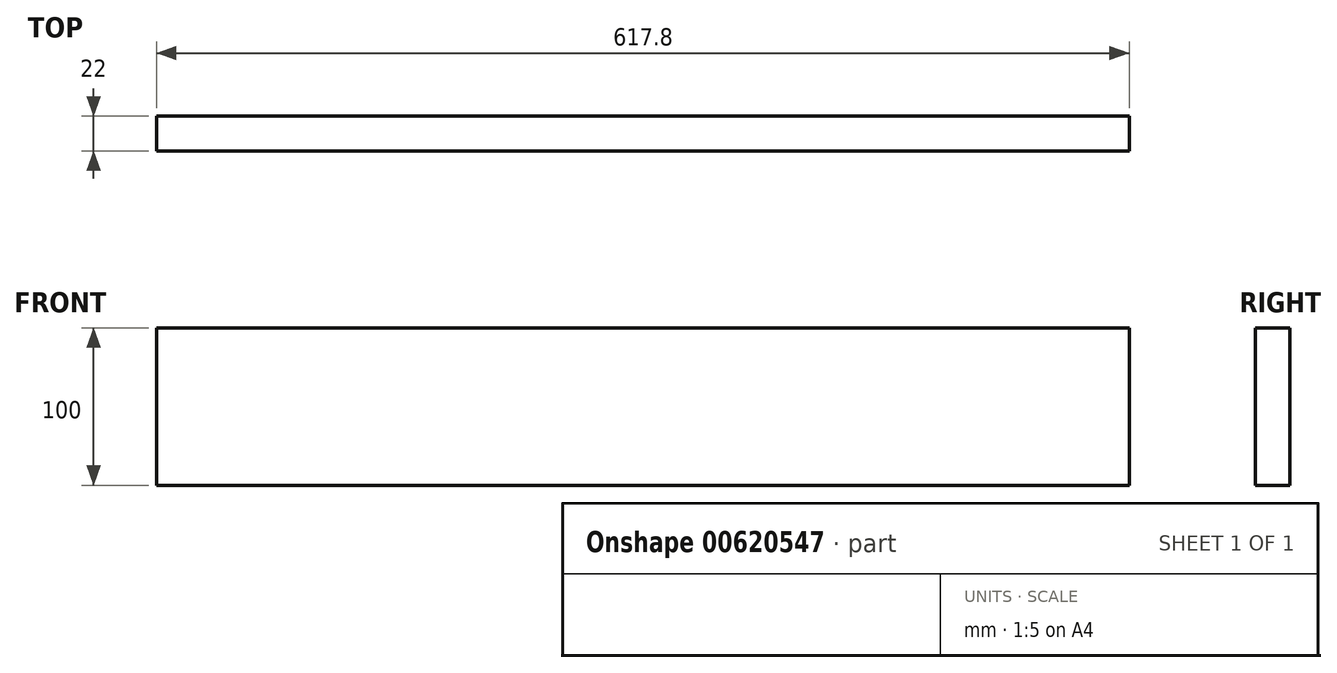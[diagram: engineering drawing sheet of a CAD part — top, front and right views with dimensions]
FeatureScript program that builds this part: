
annotation { "Feature Type Name" : "Feature", "Feature Type Description" : "" }
export const myFeature = defineFeature(function(context is Context, id is Id, definition is map)
    precondition{}
    {
        {
            var Q0;
            Q0=qCreatedBy(makeId("Front.planeOp"),FACE);
            var sketch = newSketch(context, id + "F0", { "sketchPlane" : qUnion([Q0])});
            skLineSegment(sketch, "E0.bottom", {"start": v(308.9, -50) * mm, "end": v(-308.9, -50) * mm});
            skLineSegment(sketch, "E0.top", {"start": v(308.9, 50) * mm, "end": v(-308.9, 50) * mm});
            skLineSegment(sketch, "E0.left", {"start": v(308.9, -50) * mm, "end": v(308.9, 50) * mm});
            skLineSegment(sketch, "E0.right", {"start": v(-308.9, -50) * mm, "end": v(-308.9, 50) * mm});
            skPoint(sketch, "E0.middle", {"position": v(0, 0) * mm});
            skSolve(sketch);
        }
        {
            var Q0;
            Q0=makeQuery(id+"F0.imprint","IMPRINT",FACE,{"disambiguationData":[TD([[makeQuery(id+"F0.imprint","IMPRINT",EDGE,{"derivedFrom":sQuery(id+"F0.wireOp",EDGE,"E0.bottom")}),-1.0]])]});
            extrude(context, id + "F1", {"entities" : qUnion([Q0]), "depth" : 22 * mm, "offsetDistance" : 25 * mm});
        }
    });
